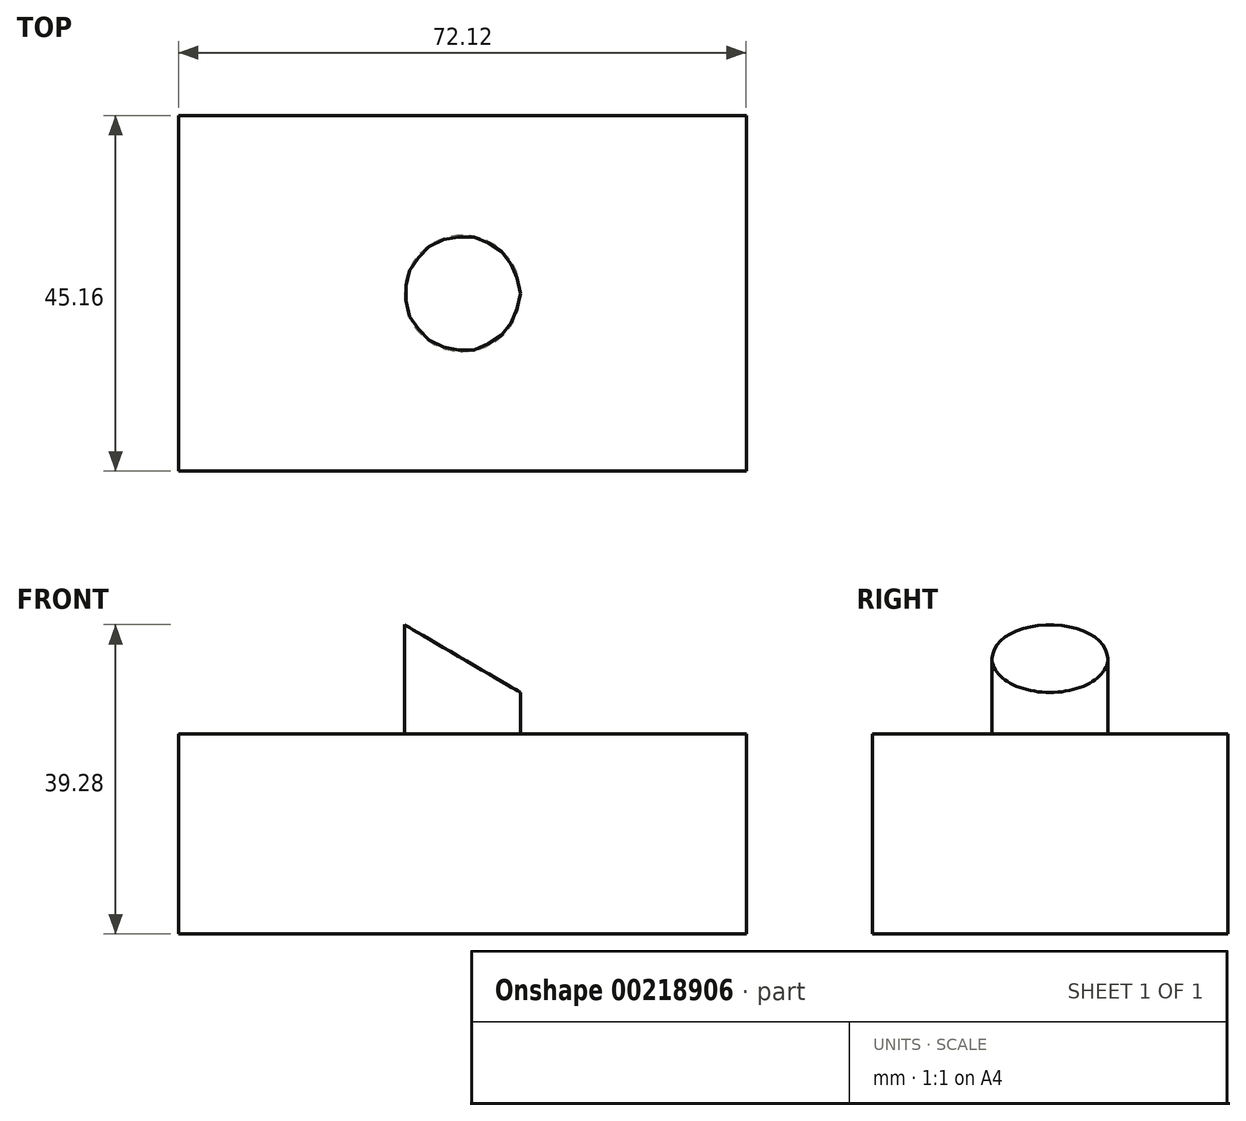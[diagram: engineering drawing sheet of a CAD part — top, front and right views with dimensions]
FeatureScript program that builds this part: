
annotation { "Feature Type Name" : "Feature", "Feature Type Description" : "" }
export const myFeature = defineFeature(function(context is Context, id is Id, definition is map)
    precondition{}
    {
        {
            var Q0;
            Q0=qCreatedBy(makeId("Top.planeOp"),FACE);
            var sketch = newSketch(context, id + "F0", { "sketchPlane" : qUnion([Q0])});
            skLineSegment(sketch, "E0.bottom", {"start": v(36.06, 22.58) * mm, "end": v(-36.06, 22.58) * mm});
            skLineSegment(sketch, "E0.top", {"start": v(36.06, -22.58) * mm, "end": v(-36.06, -22.58) * mm});
            skLineSegment(sketch, "E0.left", {"start": v(36.06, 22.58) * mm, "end": v(36.06, -22.58) * mm});
            skLineSegment(sketch, "E0.right", {"start": v(-36.06, 22.58) * mm, "end": v(-36.06, -22.58) * mm});
            skPoint(sketch, "E0.middle", {"position": v(0, 0) * mm});
            skSolve(sketch);
        }
        {
            var Q0;
            Q0=makeQuery(id+"F0.imprint","IMPRINT",FACE,{"disambiguationData":[TD([[makeQuery(id+"F0.imprint","IMPRINT",EDGE,{"derivedFrom":sQuery(id+"F0.wireOp",EDGE,"E0.bottom")}),1.0]])]});
            extrude(context, id + "F1", {"entities" : qUnion([Q0]), "depth" : 25.4 * mm});
        }
        {
            var Q0;
            Q0=makeQuery(id+"F1.opExtrude","CAP_FACE",FACE,{"disambiguationData":[OSD([sQuery(id+"F0.wireOp",EDGE,"E0.bottom"),sQuery(id+"F0.wireOp",EDGE,"E0.top"),sQuery(id+"F0.wireOp",EDGE,"E0.left"),sQuery(id+"F0.wireOp",EDGE,"E0.right")])],"isStart":false});
            var sketch = newSketch(context, id + "F2", { "sketchPlane" : qUnion([Q0])});
            skCircle(sketch, "E1", {"center": v(0, 0) * mm, "radius": 7.37 * mm});
            skSolve(sketch);
        }
        {
            var Q0;
            Q0=makeQuery(id+"F2.imprint","IMPRINT",FACE,{"disambiguationData":[TD([[makeQuery(id+"F2.imprint","IMPRINT",EDGE,{"derivedFrom":sQuery(id+"F2.wireOp",EDGE,"E1")}),1.0]])]});
            extrude(context, id + "F3", {"entities" : qUnion([Q0]), "operationType" : NewBodyOperationType.ADD, "depth" : 15 * mm});
        }
        {
            var Q0;
            Q0=makeQuery(id+"F1.opExtrude","SWEPT_FACE",FACE,{"disambiguationData":[OSD([sQuery(id+"F0.wireOp",EDGE,"E0.top")])]});
            var sketch = newSketch(context, id + "F4", { "sketchPlane" : qUnion([Q0])});
            skLineSegment(sketch, "E2", {"start": v(-11, 41.4) * mm, "end": v(10.06, 29.1) * mm});
            skLineSegment(sketch, "E3", {"start": v(10.06, 29.1) * mm, "end": v(10.06, 44.36) * mm});
            skLineSegment(sketch, "E4", {"start": v(10.06, 44.36) * mm, "end": v(-11, 41.4) * mm});
            skSolve(sketch);
        }
        {
            var Q0;
            Q0=makeQuery(id+"F4.imprint","IMPRINT",FACE,{"disambiguationData":[TD([[makeQuery(id+"F4.imprint","IMPRINT",EDGE,{"derivedFrom":sQuery(id+"F4.wireOp",EDGE,"E2")}),1.0]])]});
            extrude(context, id + "F5", {"entities" : qUnion([Q0]), "operationType" : NewBodyOperationType.REMOVE, "oppositeDirection" : true, "depth" : 41.66 * mm});
        }
    });
